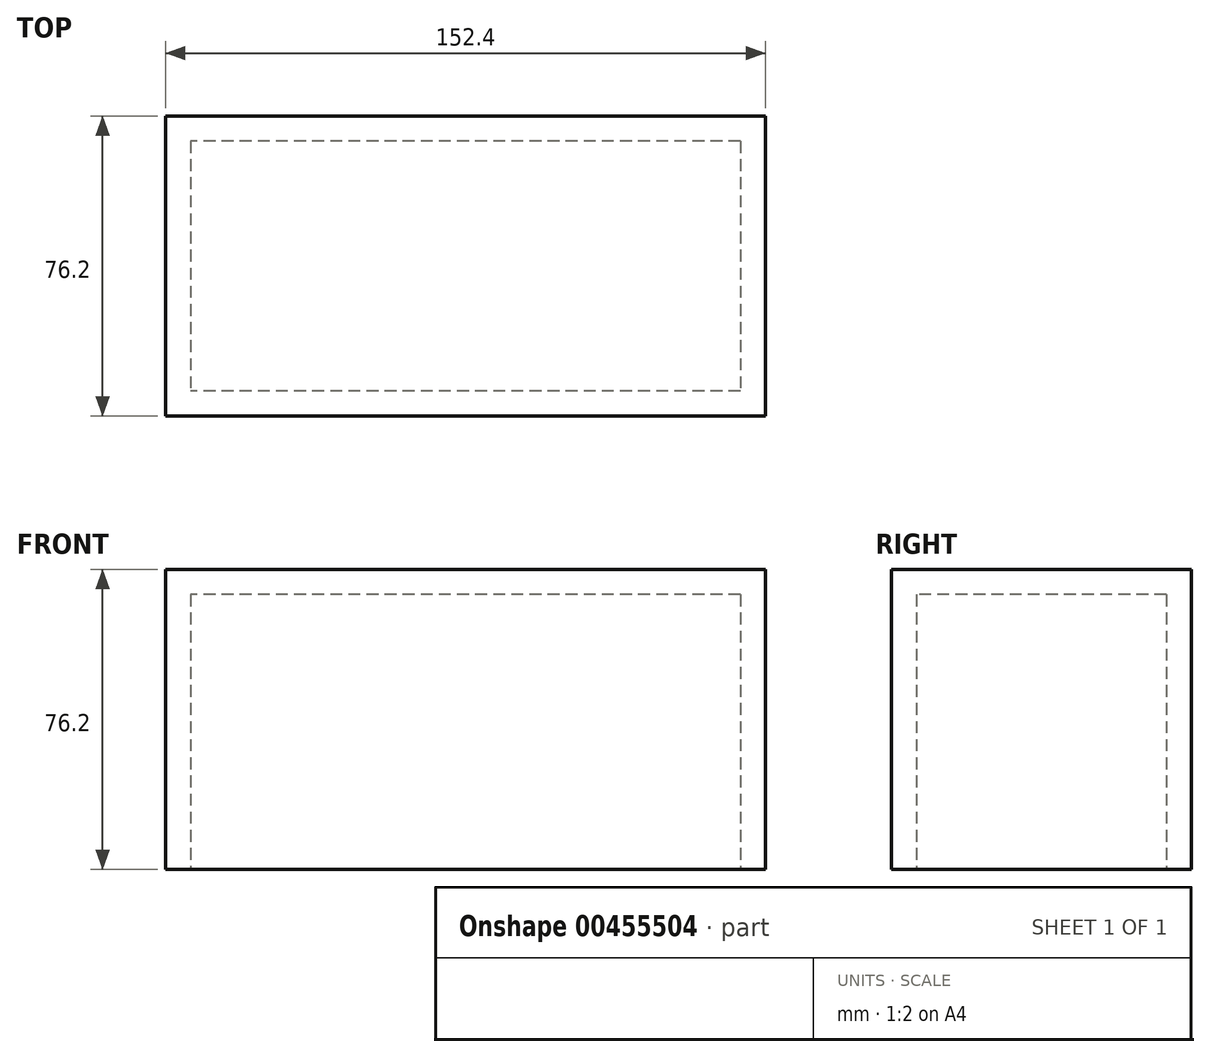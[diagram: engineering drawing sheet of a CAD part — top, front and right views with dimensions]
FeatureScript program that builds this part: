
annotation { "Feature Type Name" : "Feature", "Feature Type Description" : "" }
export const myFeature = defineFeature(function(context is Context, id is Id, definition is map)
    precondition{}
    {
        {
            var Q0;
            Q0=qCreatedBy(makeId("Top.planeOp"),FACE);
            var sketch = newSketch(context, id + "F0", { "sketchPlane" : qUnion([Q0])});
            skLineSegment(sketch, "E0.bottom", {"start": v(76.2, 38.1) * mm, "end": v(-76.2, 38.1) * mm});
            skLineSegment(sketch, "E0.top", {"start": v(76.2, -38.1) * mm, "end": v(-76.2, -38.1) * mm});
            skLineSegment(sketch, "E0.left", {"start": v(76.2, 38.1) * mm, "end": v(76.2, -38.1) * mm});
            skLineSegment(sketch, "E0.right", {"start": v(-76.2, 38.1) * mm, "end": v(-76.2, -38.1) * mm});
            skPoint(sketch, "E0.middle", {"position": v(0, 0) * mm});
            skSolve(sketch);
        }
        {
            var Q0;
            Q0 = qSketchRegion(id + "F0", true);
            extrude(context, id + "F1", {"entities" : qUnion([Q0]), "depth" : 76.2 * mm});
        }
        {
            var Q0;
            Q0=makeQuery(id+"F1.opExtrude","CAP_FACE",FACE,{"disambiguationData":[OSD([sQuery(id+"F0.wireOp",EDGE,"E0.bottom"),sQuery(id+"F0.wireOp",EDGE,"E0.top"),sQuery(id+"F0.wireOp",EDGE,"E0.left"),sQuery(id+"F0.wireOp",EDGE,"E0.right")])],"isStart":true});
            shell(context, id + "F2", {"entities" : qUnion([Q0]), "thickness" : 6.35 * mm});
        }
        {
            var Q0;
            Q0=qCreatedBy(makeId("Top.planeOp"),FACE);
            var sketch = newSketch(context, id + "F3", { "sketchPlane" : qUnion([Q0])});
            skLineSegment(sketch, "E1.bottom", {"start": v(76.2, 38.1) * mm, "end": v(-76.2, 38.1) * mm});
            skLineSegment(sketch, "E1.top", {"start": v(76.2, -38.1) * mm, "end": v(-76.2, -38.1) * mm});
            skLineSegment(sketch, "E1.left", {"start": v(76.2, 38.1) * mm, "end": v(76.2, -38.1) * mm});
            skLineSegment(sketch, "E1.right", {"start": v(-76.2, 38.1) * mm, "end": v(-76.2, -38.1) * mm});
            skPoint(sketch, "E1.middle", {"position": v(0, 0) * mm});
            skSolve(sketch);
        }
        {
            var Q0;
            Q0 = qSketchRegion(id + "F3", true);
            extrude(context, id + "F4", {"entities" : qUnion([Q0]), "depth" : 1 / 50.8 * mm});
        }
    });
